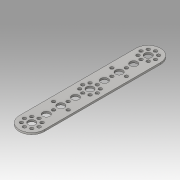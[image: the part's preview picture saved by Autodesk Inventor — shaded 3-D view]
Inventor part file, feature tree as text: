
AUTODESK INVENTOR PART (.ipt)
format: ipt  version: 2016 (Build 200138000, 138)  size: 176,640 bytes
history: native  units: in
note: dims shown in document units (in); Inventor stores cm internally (conversion verified against a paired STEP export)
features: extrude x1, sketch x1
ambient origin geometry x8: Origin, YZ Plane, XZ Plane, XY Plane, X Axis, Y Axis, Z Axis, Center Point
bodies: Solid1 (feature_tree)
feature tree (2):
  extrude  "Extrusion1"  [1 undecoded]
  sketch  "Sketch1"  dims[d0=0.0787in d1=0.0in]
note: 1 required parameter value undecoded (feature->parameter linkage not recoverable at this tier; creation-order binding heuristic only, values carry confidence <= 0.55)
